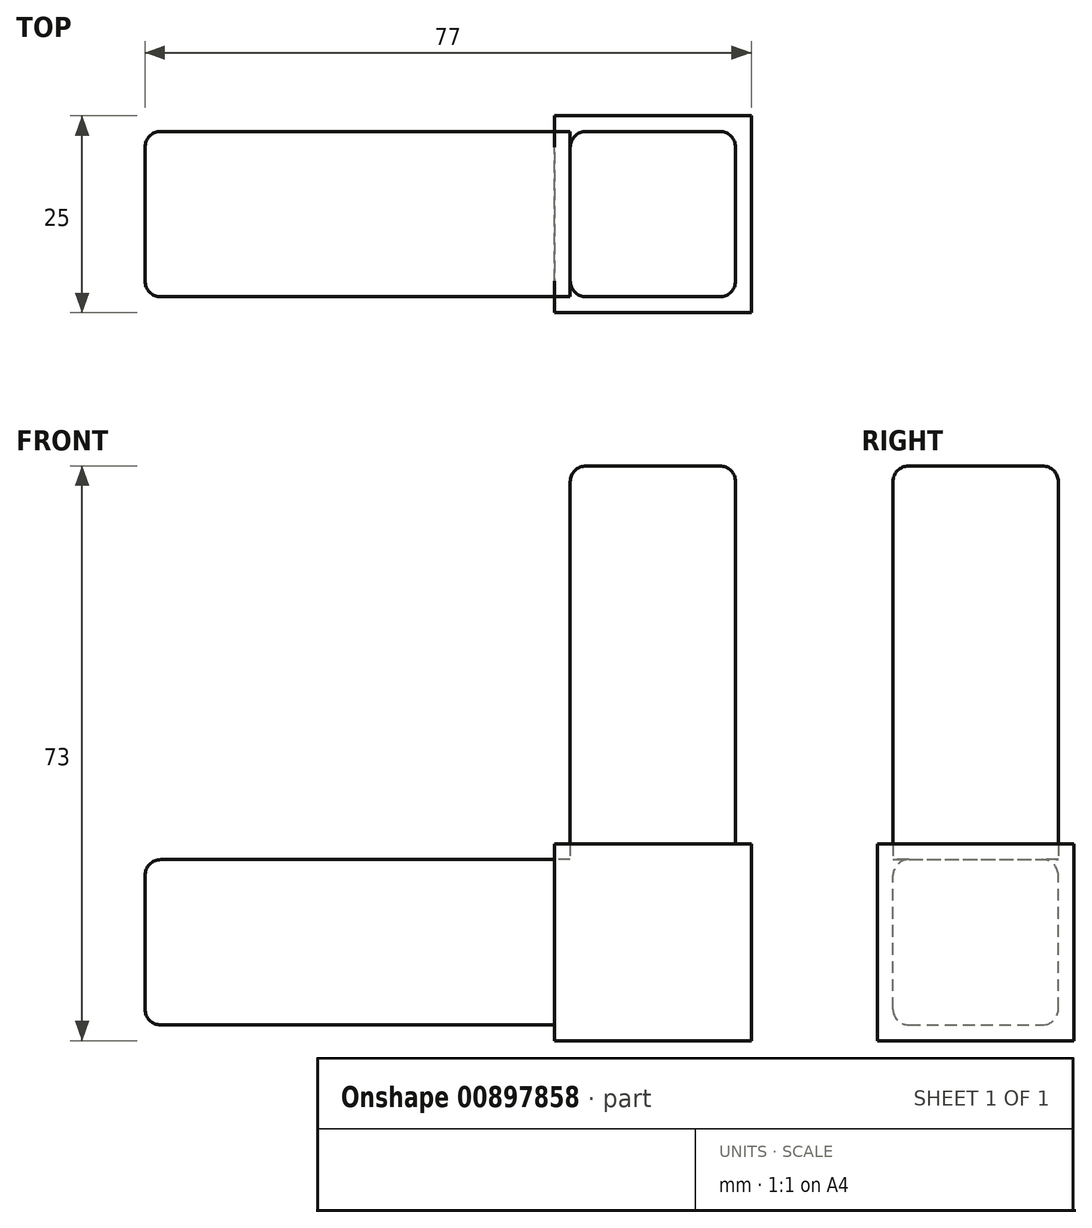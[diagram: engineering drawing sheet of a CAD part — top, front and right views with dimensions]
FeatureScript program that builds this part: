
annotation { "Feature Type Name" : "Feature", "Feature Type Description" : "" }
export const myFeature = defineFeature(function(context is Context, id is Id, definition is map)
    precondition{}
    {
        {
            var Q0;
            Q0=qCreatedBy(makeId("Front.planeOp"),FACE);
            var sketch = newSketch(context, id + "F0", { "sketchPlane" : qUnion([Q0])});
            skLineSegment(sketch, "E0.bottom", {"start": v(37.5, -10.5) * mm, "end": v(-37.5, -10.5) * mm});
            skLineSegment(sketch, "E0.top", {"start": v(16.5, 10.5) * mm, "end": v(-37.5, 10.5) * mm});
            skLineSegment(sketch, "E0.left", {"start": v(37.5, -10.5) * mm, "end": v(37.5, 10.5) * mm});
            skLineSegment(sketch, "E0.right", {"start": v(-37.5, -10.5) * mm, "end": v(-37.5, 10.5) * mm});
            skPoint(sketch, "E0.middle", {"position": v(0, 0) * mm});
            skLineSegment(sketch, "E1", {"start": v(37.5, 10.5) * mm, "end": v(37.5, 60.5) * mm});
            skLineSegment(sketch, "E2", {"start": v(37.5, 60.5) * mm, "end": v(16.5, 60.5) * mm});
            skLineSegment(sketch, "E3", {"start": v(16.5, 60.5) * mm, "end": v(16.5, 10.5) * mm});
            skLineSegment(sketch, "E4", {"start": v(16.5, 10.5) * mm, "end": v(37.5, -10.5) * mm, "construction": true});
            skLineSegment(sketch, "E5", {"start": v(37.5, 10.5) * mm, "end": v(16.5, -10.5) * mm, "construction": true});
            skLineSegment(sketch, "E6.bottom", {"start": v(39.5, -12.5) * mm, "end": v(14.5, -12.5) * mm});
            skLineSegment(sketch, "E6.top", {"start": v(39.5, 12.5) * mm, "end": v(14.5, 12.5) * mm});
            skLineSegment(sketch, "E6.left", {"start": v(39.5, -12.5) * mm, "end": v(39.5, 12.5) * mm});
            skLineSegment(sketch, "E6.right", {"start": v(14.5, -12.5) * mm, "end": v(14.5, 12.5) * mm});
            skPoint(sketch, "E6.middle", {"position": v(27, 0) * mm});
            skSolve(sketch);
        }
        {
            var Q0;
            {var subQ0=sQuery(id+"F0.wireOp",EDGE,"E2");Q0=makeQuery(id+"F0.imprint","IMPRINT",FACE,{"disambiguationData":[TD([[makeQuery(id+"F0.imprint","IMPRINT",EDGE,{"derivedFrom":subQ0}),1.0]])]});}
            var Q1;
            {var subQ0=sQuery(id+"F0.wireOp",EDGE,"E0.right");Q1=makeQuery(id+"F0.imprint","IMPRINT",FACE,{"disambiguationData":[TD([[makeQuery(id+"F0.imprint","IMPRINT",EDGE,{"derivedFrom":subQ0}),-1.0]])]});}
            var Q2;
            {var subQ1=sQuery(id+"F0.wireOp",EDGE,"E0.left");Q2=makeQuery(id+"F0.imprint","IMPRINT",FACE,{"disambiguationData":[TD([[makeQuery(id+"F0.imprint","IMPRINT",EDGE,{"derivedFrom":subQ1}),1.0]])]});}
            extrude(context, id + "F1", {"entities" : qUnion([Q0, Q1, Q2]), "depth" : 21 * mm, "offsetDistance" : 25 * mm});
        }
        {
            var Q0;
            {var subQ1=sQuery(id+"F0.wireOp",EDGE,"E0.left");Q0=makeQuery(id+"F0.imprint","IMPRINT",FACE,{"disambiguationData":[TD([[makeQuery(id+"F0.imprint","IMPRINT",EDGE,{"derivedFrom":subQ1}),-1.0]])]});}
            var Q1;
            {var subQ0=sQuery(id+"F0.wireOp",EDGE,"E3");var subQ1=sQuery(id+"F0.wireOp",EDGE,"E0.top");var subQ2=makeQuery(id+"F0.imprint","INTERSECT",VERTEX,{"derivedFrom":[subQ1,subQ0]});Q1=makeQuery(id+"F0.imprint","IMPRINT",FACE,{"disambiguationData":[TD([[makeQuery(id+"F0.imprint","IMPRINT",EDGE,{"disambiguationData":[TD([[subQ2,-1.0]])],"derivedFrom":subQ1}),-1.0]])]});}
            var Q2;
            {var subQ1=sQuery(id+"F0.wireOp",EDGE,"E0.left");Q2=makeQuery(id+"F0.imprint","IMPRINT",FACE,{"disambiguationData":[TD([[makeQuery(id+"F0.imprint","IMPRINT",EDGE,{"derivedFrom":subQ1}),1.0]])]});}
            extrude(context, id + "F2", {"entities" : qUnion([Q0, Q1, Q2]), "operationType" : NewBodyOperationType.ADD, "oppositeDirection" : true, "depth" : 2 * mm, "offsetDistance" : 25 * mm});
        }
        {
            var Q0;
            Q0=makeQuery(id+"F1.opExtrude","CAP_FACE",FACE,{"disambiguationData":[OSD([sQuery(id+"F0.wireOp",EDGE,"E0.bottom"),sQuery(id+"F0.wireOp",EDGE,"E0.top"),sQuery(id+"F0.wireOp",EDGE,"E0.left"),sQuery(id+"F0.wireOp",EDGE,"E0.right"),sQuery(id+"F0.wireOp",EDGE,"E1"),sQuery(id+"F0.wireOp",EDGE,"E2"),sQuery(id+"F0.wireOp",EDGE,"E3")])],"isStart":false});
            var sketch = newSketch(context, id + "F3", { "sketchPlane" : qUnion([Q0])});
            skPoint(sketch, "E7.0", {"position": v(14.5, 12.5) * mm});
            skPoint(sketch, "E8.0", {"position": v(39.5, 12.5) * mm});
            skPoint(sketch, "E9.0", {"position": v(39.5, -12.5) * mm});
            skPoint(sketch, "E10.0", {"position": v(14.5, -12.5) * mm});
            skLineSegment(sketch, "E11.bottom", {"start": v(14.5, 12.5) * mm, "end": v(39.5, 12.5) * mm});
            skLineSegment(sketch, "E11.top", {"start": v(14.5, -12.5) * mm, "end": v(39.5, -12.5) * mm});
            skLineSegment(sketch, "E11.left", {"start": v(14.5, 12.5) * mm, "end": v(14.5, -12.5) * mm});
            skLineSegment(sketch, "E11.right", {"start": v(39.5, 12.5) * mm, "end": v(39.5, -12.5) * mm});
            skSolve(sketch);
        }
        {
            var Q0;
            Q0 = qSketchRegion(id + "F3", true);
            extrude(context, id + "F4", {"entities" : qUnion([Q0]), "operationType" : NewBodyOperationType.ADD, "depth" : 2 * mm, "offsetDistance" : 25 * mm});
        }
        {
            var Q0;
            Q0=makeQuery(id+"F1.opExtrude","SWEPT_FACE",FACE,{"disambiguationData":[OSD([sQuery(id+"F0.wireOp",EDGE,"E0.left"),sQuery(id+"F0.wireOp",EDGE,"E1")])]});
            var sketch = newSketch(context, id + "F5", { "sketchPlane" : qUnion([Q0])});
            skPoint(sketch, "E12.0", {"position": v(-23, 12.5) * mm});
            skPoint(sketch, "E13.0", {"position": v(2, 12.5) * mm});
            skPoint(sketch, "E14.0", {"position": v(2, -12.5) * mm});
            skPoint(sketch, "E15.0", {"position": v(-23, -12.5) * mm});
            skLineSegment(sketch, "E16.bottom", {"start": v(-23, 12.5) * mm, "end": v(2, 12.5) * mm});
            skLineSegment(sketch, "E16.top", {"start": v(-23, -12.5) * mm, "end": v(2, -12.5) * mm});
            skLineSegment(sketch, "E16.left", {"start": v(-23, 12.5) * mm, "end": v(-23, -12.5) * mm});
            skLineSegment(sketch, "E16.right", {"start": v(2, 12.5) * mm, "end": v(2, -12.5) * mm});
            skSolve(sketch);
        }
        {
            var Q0;
            Q0 = qSketchRegion(id + "F5", true);
            extrude(context, id + "F6", {"entities" : qUnion([Q0]), "operationType" : NewBodyOperationType.ADD, "depth" : 2 * mm, "offsetDistance" : 25 * mm});
        }
        {
            var Q0;
            Q0=makeQuery(id+"F1.opExtrude","SWEPT_FACE",FACE,{"disambiguationData":[OSD([sQuery(id+"F0.wireOp",EDGE,"E0.bottom")])]});
            var sketch = newSketch(context, id + "F7", { "sketchPlane" : qUnion([Q0])});
            skPoint(sketch, "E17.0", {"position": v(14.5, 23) * mm});
            skPoint(sketch, "E18.0", {"position": v(39.5, 23) * mm});
            skPoint(sketch, "E19.0", {"position": v(39.5, -2) * mm});
            skPoint(sketch, "E20.0", {"position": v(14.5, -2) * mm});
            skLineSegment(sketch, "E21.bottom", {"start": v(14.5, 23) * mm, "end": v(39.5, 23) * mm});
            skLineSegment(sketch, "E21.top", {"start": v(14.5, -2) * mm, "end": v(39.5, -2) * mm});
            skLineSegment(sketch, "E21.left", {"start": v(14.5, 23) * mm, "end": v(14.5, -2) * mm});
            skLineSegment(sketch, "E21.right", {"start": v(39.5, 23) * mm, "end": v(39.5, -2) * mm});
            skSolve(sketch);
        }
        {
            var Q0;
            Q0 = qSketchRegion(id + "F7", true);
            extrude(context, id + "F8", {"entities" : qUnion([Q0]), "operationType" : NewBodyOperationType.ADD, "depth" : 2 * mm, "offsetDistance" : 25 * mm});
        }
        {
            var Q0;
            Q0=makeQuery(id+"F1.opExtrude","SWEPT_EDGE",EDGE,{"disambiguationData":[OSD([sQuery(id+"F0.wireOp",EDGE,"E0.bottom"),sQuery(id+"F0.wireOp",EDGE,"E0.right")])]});
            var Q1;
            Q1=makeQuery(id+"F1.opExtrude","CAP_EDGE",EDGE,{"disambiguationData":[OSD([sQuery(id+"F0.wireOp",EDGE,"E0.right")])],"isStart":true});
            var Q2;
            Q2=makeQuery(id+"F1.opExtrude","SWEPT_EDGE",EDGE,{"disambiguationData":[OSD([sQuery(id+"F0.wireOp",EDGE,"E0.top"),sQuery(id+"F0.wireOp",EDGE,"E0.right")])]});
            var Q3;
            Q3=makeQuery(id+"F1.opExtrude","CAP_EDGE",EDGE,{"disambiguationData":[OSD([sQuery(id+"F0.wireOp",EDGE,"E0.right")])],"isStart":false});
            var Q4;
            Q4=makeQuery(id+"F1.opExtrude","CAP_EDGE",EDGE,{"disambiguationData":[OSD([sQuery(id+"F0.wireOp",EDGE,"E2")])],"isStart":true});
            var Q5;
            Q5=makeQuery(id+"F1.opExtrude","SWEPT_EDGE",EDGE,{"disambiguationData":[OSD([sQuery(id+"F0.wireOp",EDGE,"E2"),sQuery(id+"F0.wireOp",EDGE,"E3")])]});
            var Q6;
            Q6=makeQuery(id+"F1.opExtrude","SWEPT_EDGE",EDGE,{"disambiguationData":[OSD([sQuery(id+"F0.wireOp",EDGE,"E1"),sQuery(id+"F0.wireOp",EDGE,"E2")])]});
            var Q7;
            Q7=makeQuery(id+"F1.opExtrude","CAP_EDGE",EDGE,{"disambiguationData":[OSD([sQuery(id+"F0.wireOp",EDGE,"E2")])],"isStart":false});
            var Q8;
            {var subQ0=sQuery(id+"F0.wireOp",EDGE,"E3");Q8=makeQuery(id+"F4.boolean.opBoolean","SPLIT",EDGE,{"disambiguationData":[topologyDisambiguationEdgeConnected([makeQuery(id+"F1.opExtrude","CAP_FACE",FACE,{"disambiguationData":[OSD([sQuery(id+"F0.wireOp",EDGE,"E0.bottom"),sQuery(id+"F0.wireOp",EDGE,"E0.top"),sQuery(id+"F0.wireOp",EDGE,"E0.left"),sQuery(id+"F0.wireOp",EDGE,"E0.right"),sQuery(id+"F0.wireOp",EDGE,"E1"),sQuery(id+"F0.wireOp",EDGE,"E2"),subQ0])],"isStart":false})])],"derivedFrom":makeQuery(id+"F1.opExtrude","CAP_EDGE",EDGE,{"disambiguationData":[OSD([subQ0])],"isStart":false})});}
            var Q9;
            {var subQ0=sQuery(id+"F0.wireOp",EDGE,"E1");var subQ1=sQuery(id+"F0.wireOp",EDGE,"E0.left");Q9=makeQuery(id+"F4.boolean.opBoolean","SPLIT",EDGE,{"disambiguationData":[topologyDisambiguationEdgeConnected([makeQuery(id+"F1.opExtrude","CAP_FACE",FACE,{"disambiguationData":[OSD([sQuery(id+"F0.wireOp",EDGE,"E0.bottom"),sQuery(id+"F0.wireOp",EDGE,"E0.top"),subQ1,sQuery(id+"F0.wireOp",EDGE,"E0.right"),subQ0,sQuery(id+"F0.wireOp",EDGE,"E2"),sQuery(id+"F0.wireOp",EDGE,"E3")])],"isStart":false})])],"derivedFrom":makeQuery(id+"F1.opExtrude","CAP_EDGE",EDGE,{"disambiguationData":[OSD([subQ1,subQ0])],"isStart":false})});}
            var Q10;
            {var subQ0=sQuery(id+"F0.wireOp",EDGE,"E1");var subQ1=sQuery(id+"F0.wireOp",EDGE,"E0.left");Q10=makeQuery(id+"F2.boolean.opBoolean","SPLIT",EDGE,{"disambiguationData":[topologyDisambiguationEdgeConnected([makeQuery(id+"F1.opExtrude","CAP_FACE",FACE,{"disambiguationData":[OSD([sQuery(id+"F0.wireOp",EDGE,"E0.bottom"),sQuery(id+"F0.wireOp",EDGE,"E0.top"),subQ1,sQuery(id+"F0.wireOp",EDGE,"E0.right"),subQ0,sQuery(id+"F0.wireOp",EDGE,"E2"),sQuery(id+"F0.wireOp",EDGE,"E3")])],"isStart":true})])],"derivedFrom":makeQuery(id+"F1.opExtrude","CAP_EDGE",EDGE,{"disambiguationData":[OSD([subQ1,subQ0])],"isStart":true})});}
            var Q11;
            {var subQ0=sQuery(id+"F0.wireOp",EDGE,"E3");Q11=makeQuery(id+"F2.boolean.opBoolean","SPLIT",EDGE,{"disambiguationData":[topologyDisambiguationEdgeConnected([makeQuery(id+"F1.opExtrude","CAP_FACE",FACE,{"disambiguationData":[OSD([sQuery(id+"F0.wireOp",EDGE,"E0.bottom"),sQuery(id+"F0.wireOp",EDGE,"E0.top"),sQuery(id+"F0.wireOp",EDGE,"E0.left"),sQuery(id+"F0.wireOp",EDGE,"E0.right"),sQuery(id+"F0.wireOp",EDGE,"E1"),sQuery(id+"F0.wireOp",EDGE,"E2"),subQ0])],"isStart":true})])],"derivedFrom":makeQuery(id+"F1.opExtrude","CAP_EDGE",EDGE,{"disambiguationData":[OSD([subQ0])],"isStart":true})});}
            var Q12;
            {var subQ0=sQuery(id+"F0.wireOp",EDGE,"E0.top");Q12=makeQuery(id+"F2.boolean.opBoolean","SPLIT",EDGE,{"disambiguationData":[topologyDisambiguationEdgeConnected([makeQuery(id+"F1.opExtrude","CAP_FACE",FACE,{"disambiguationData":[OSD([sQuery(id+"F0.wireOp",EDGE,"E0.bottom"),subQ0,sQuery(id+"F0.wireOp",EDGE,"E0.left"),sQuery(id+"F0.wireOp",EDGE,"E0.right"),sQuery(id+"F0.wireOp",EDGE,"E1"),sQuery(id+"F0.wireOp",EDGE,"E2"),sQuery(id+"F0.wireOp",EDGE,"E3")])],"isStart":true})])],"derivedFrom":makeQuery(id+"F1.opExtrude","CAP_EDGE",EDGE,{"disambiguationData":[OSD([subQ0])],"isStart":true})});}
            var Q13;
            {var subQ0=sQuery(id+"F0.wireOp",EDGE,"E0.bottom");Q13=makeQuery(id+"F2.boolean.opBoolean","SPLIT",EDGE,{"disambiguationData":[topologyDisambiguationEdgeConnected([makeQuery(id+"F1.opExtrude","CAP_FACE",FACE,{"disambiguationData":[OSD([subQ0,sQuery(id+"F0.wireOp",EDGE,"E0.top"),sQuery(id+"F0.wireOp",EDGE,"E0.left"),sQuery(id+"F0.wireOp",EDGE,"E0.right"),sQuery(id+"F0.wireOp",EDGE,"E1"),sQuery(id+"F0.wireOp",EDGE,"E2"),sQuery(id+"F0.wireOp",EDGE,"E3")])],"isStart":true})])],"derivedFrom":makeQuery(id+"F1.opExtrude","CAP_EDGE",EDGE,{"disambiguationData":[OSD([subQ0])],"isStart":true})});}
            var Q14;
            {var subQ0=sQuery(id+"F0.wireOp",EDGE,"E0.top");Q14=makeQuery(id+"F4.boolean.opBoolean","SPLIT",EDGE,{"disambiguationData":[topologyDisambiguationEdgeConnected([makeQuery(id+"F1.opExtrude","CAP_FACE",FACE,{"disambiguationData":[OSD([sQuery(id+"F0.wireOp",EDGE,"E0.bottom"),subQ0,sQuery(id+"F0.wireOp",EDGE,"E0.left"),sQuery(id+"F0.wireOp",EDGE,"E0.right"),sQuery(id+"F0.wireOp",EDGE,"E1"),sQuery(id+"F0.wireOp",EDGE,"E2"),sQuery(id+"F0.wireOp",EDGE,"E3")])],"isStart":false})])],"derivedFrom":makeQuery(id+"F1.opExtrude","CAP_EDGE",EDGE,{"disambiguationData":[OSD([subQ0])],"isStart":false})});}
            var Q15;
            {var subQ0=sQuery(id+"F0.wireOp",EDGE,"E0.bottom");Q15=makeQuery(id+"F4.boolean.opBoolean","SPLIT",EDGE,{"disambiguationData":[topologyDisambiguationEdgeConnected([makeQuery(id+"F1.opExtrude","CAP_FACE",FACE,{"disambiguationData":[OSD([subQ0,sQuery(id+"F0.wireOp",EDGE,"E0.top"),sQuery(id+"F0.wireOp",EDGE,"E0.left"),sQuery(id+"F0.wireOp",EDGE,"E0.right"),sQuery(id+"F0.wireOp",EDGE,"E1"),sQuery(id+"F0.wireOp",EDGE,"E2"),sQuery(id+"F0.wireOp",EDGE,"E3")])],"isStart":false})])],"derivedFrom":makeQuery(id+"F1.opExtrude","CAP_EDGE",EDGE,{"disambiguationData":[OSD([subQ0])],"isStart":false})});}
            fillet(context, id + "F9", {"entities" : qUnion([Q0, Q1, Q2, Q3, Q4, Q5, Q6, Q7, Q8, Q9, Q10, Q11, Q12, Q13, Q14, Q15]), "radius" : 2 * mm, "tangentPropagation" : true, "allowEdgeOverflow" : false});
        }
    });
